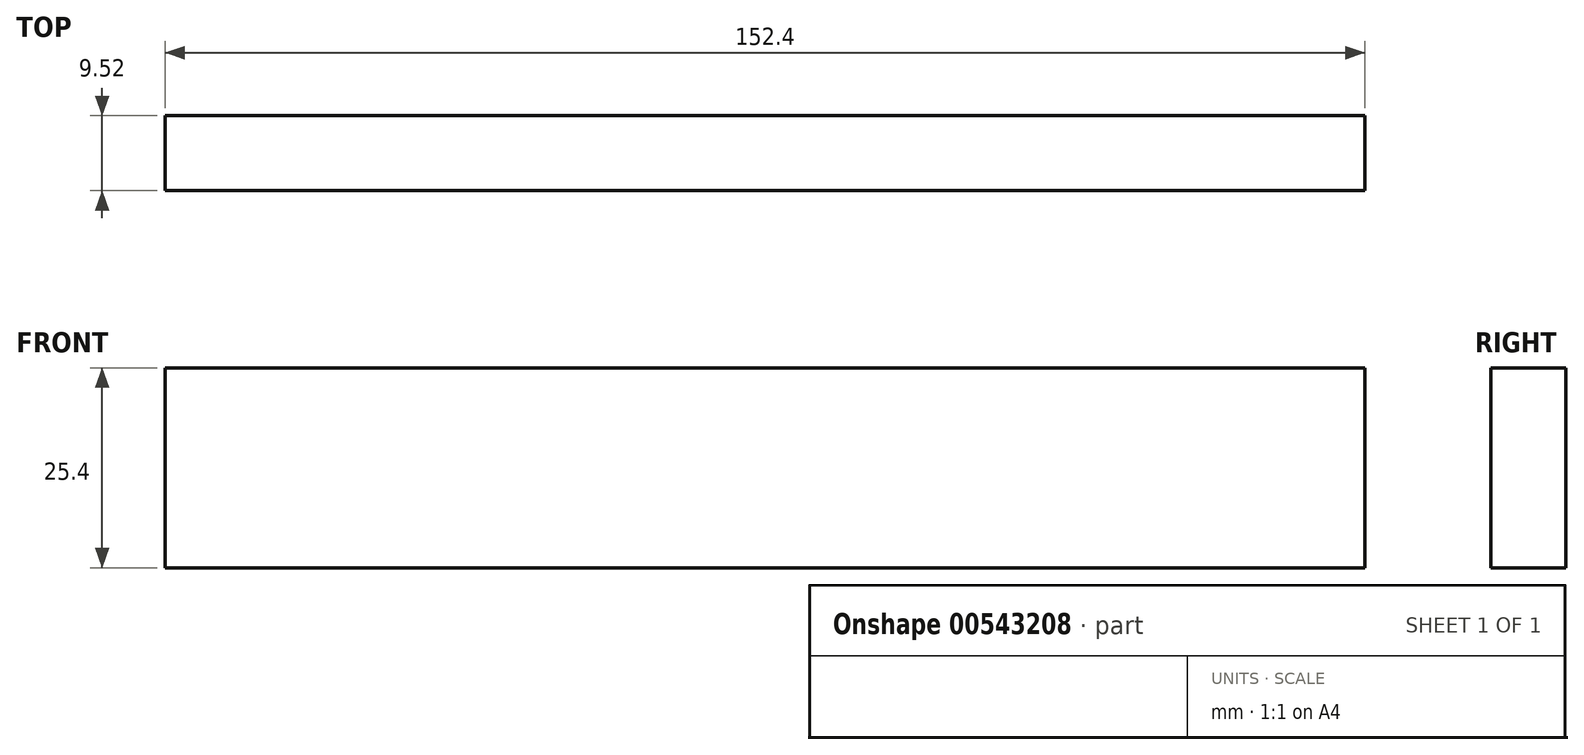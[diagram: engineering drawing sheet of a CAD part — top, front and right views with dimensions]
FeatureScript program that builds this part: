
annotation { "Feature Type Name" : "Feature", "Feature Type Description" : "" }
export const myFeature = defineFeature(function(context is Context, id is Id, definition is map)
    precondition{}
    {
        {
            var Q0;
            Q0=qCreatedBy(makeId("Front.planeOp"),FACE);
            var sketch = newSketch(context, id + "F0", { "sketchPlane" : qUnion([Q0])});
            skLineSegment(sketch, "E0.bottom", {"start": v(76.2, 12.7) * mm, "end": v(-76.2, 12.7) * mm});
            skLineSegment(sketch, "E0.top", {"start": v(76.2, -12.7) * mm, "end": v(-76.2, -12.7) * mm});
            skLineSegment(sketch, "E0.left", {"start": v(76.2, 12.7) * mm, "end": v(76.2, -12.7) * mm});
            skLineSegment(sketch, "E0.right", {"start": v(-76.2, 12.7) * mm, "end": v(-76.2, -12.7) * mm});
            skPoint(sketch, "E0.middle", {"position": v(0, 0) * mm});
            skSolve(sketch);
        }
        {
            var Q0;
            Q0 = qSketchRegion(id + "F0", true);
            extrude(context, id + "F1", {"entities" : qUnion([Q0]), "depth" : 9.52 * mm, "offsetDistance" : 25.4 * mm, "symmetric" : true});
        }
    });
